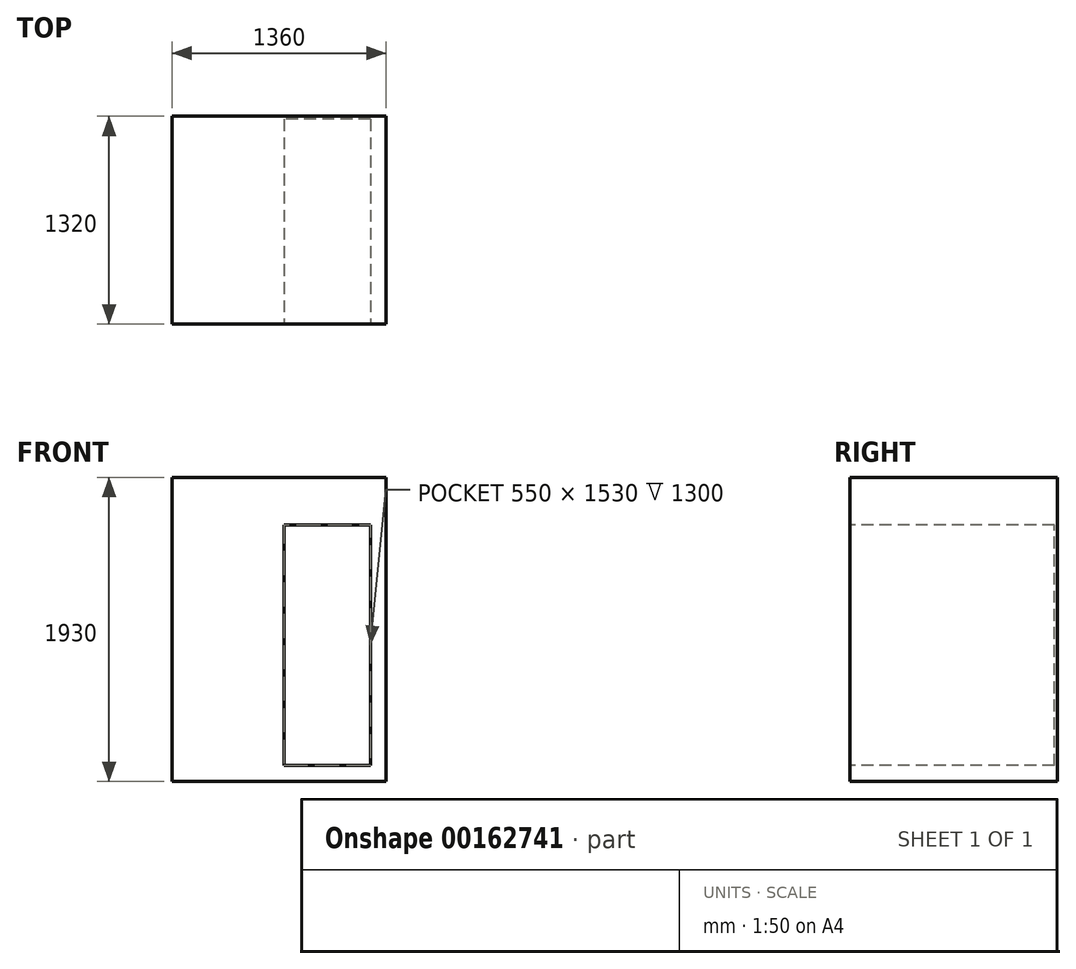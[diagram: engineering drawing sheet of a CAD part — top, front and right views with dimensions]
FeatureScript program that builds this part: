
annotation { "Feature Type Name" : "Feature", "Feature Type Description" : "" }
export const myFeature = defineFeature(function(context is Context, id is Id, definition is map)
    precondition{}
    {
        {
            var Q0;
            Q0=qCreatedBy(makeId("Front.planeOp"),FACE);
            var sketch = newSketch(context, id + "F0", { "sketchPlane" : qUnion([Q0])});
            skLineSegment(sketch, "E0.bottom", {"start": v(0, 0) * mm, "end": v(1360, 0) * mm});
            skLineSegment(sketch, "E0.top", {"start": v(0, 1930) * mm, "end": v(1360, 1930) * mm});
            skLineSegment(sketch, "E0.left", {"start": v(0, 0) * mm, "end": v(0, 1930) * mm});
            skLineSegment(sketch, "E0.right", {"start": v(1360, 0) * mm, "end": v(1360, 1930) * mm});
            skSolve(sketch);
        }
        {
            var Q0;
            Q0 = qSketchRegion(id + "F0", true);
            extrude(context, id + "F1", {"entities" : qUnion([Q0]), "depth" : 1320 * mm});
        }
        {
            var Q0;
            Q0=makeQuery(id+"F1.opExtrude","CAP_FACE",FACE,{"disambiguationData":[OSD([sQuery(id+"F0.wireOp",EDGE,"E0.bottom"),sQuery(id+"F0.wireOp",EDGE,"E0.top"),sQuery(id+"F0.wireOp",EDGE,"E0.left"),sQuery(id+"F0.wireOp",EDGE,"E0.right")])],"isStart":false});
            var sketch = newSketch(context, id + "F2", { "sketchPlane" : qUnion([Q0])});
            skLineSegment(sketch, "E1.bottom", {"start": v(1260, 100) * mm, "end": v(710, 100) * mm});
            skLineSegment(sketch, "E1.top", {"start": v(1260, 1630) * mm, "end": v(710, 1630) * mm});
            skLineSegment(sketch, "E1.left", {"start": v(1260, 100) * mm, "end": v(1260, 1630) * mm});
            skLineSegment(sketch, "E1.right", {"start": v(710, 100) * mm, "end": v(710, 1630) * mm});
            skSolve(sketch);
        }
        {
            var Q0;
            Q0 = qSketchRegion(id + "F2", true);
            extrude(context, id + "F3", {"entities" : qUnion([Q0]), "operationType" : NewBodyOperationType.REMOVE, "oppositeDirection" : true, "depth" : 1300 * mm});
        }
    });
